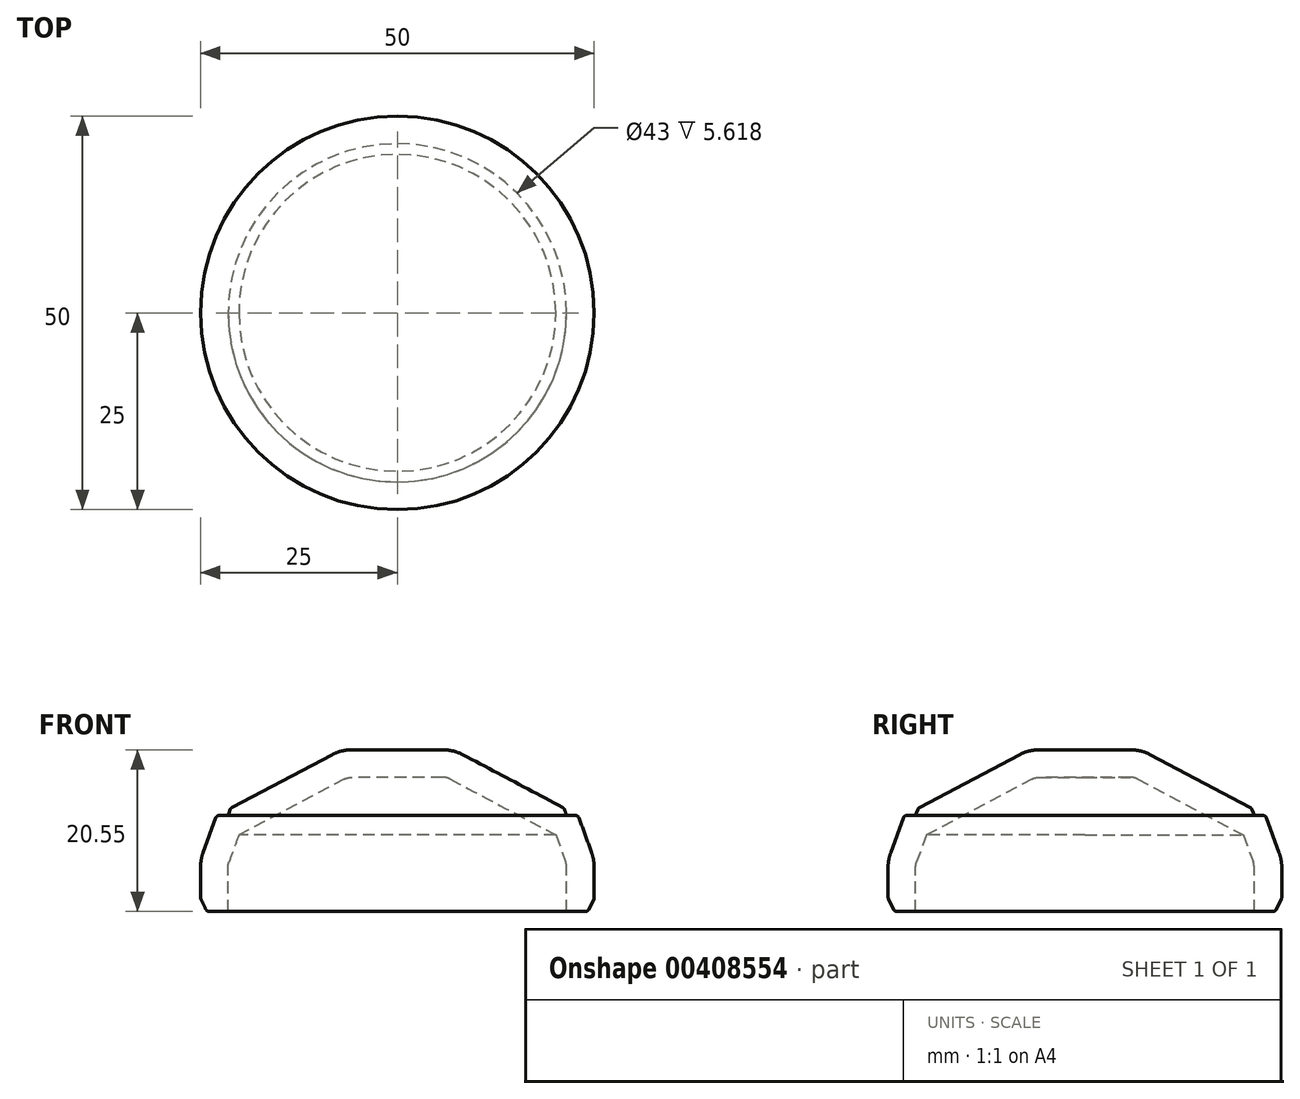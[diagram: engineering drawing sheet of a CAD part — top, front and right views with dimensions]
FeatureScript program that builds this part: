
annotation { "Feature Type Name" : "Feature", "Feature Type Description" : "" }
export const myFeature = defineFeature(function(context is Context, id is Id, definition is map)
    precondition{}
    {
        {
            var Q0;
            Q0=qCreatedBy(makeId("Front.planeOp"),FACE);
            var sketch = newSketch(context, id + "F0", { "sketchPlane" : qUnion([Q0])});
            skLineSegment(sketch, "E0", {"start": v(0, 22.04) * mm, "end": v(0, -27.86) * mm, "construction": true});
            skLineSegment(sketch, "E1", {"start": v(0, 0) * mm, "end": v(-5.75, 0) * mm});
            skArc(sketch, "E2", {"start": v(-5.75, 0) * mm, "mid": v(-7.07, -0.16) * mm, "end": v(-8.31, -0.63) * mm});
            skLineSegment(sketch, "E3", {"start": v(-8.31, -0.63) * mm, "end": v(-20.98, -7.3) * mm});
            skLineSegment(sketch, "E4", {"start": v(-23.08, -8.68) * mm, "end": v(-24.67, -13.05) * mm});
            skLineSegment(sketch, "E5", {"start": v(-25, -14.93) * mm, "end": v(-25, -20.55) * mm});
            skLineSegment(sketch, "E6", {"start": v(-25, -20.55) * mm, "end": v(0, -20.55) * mm});
            skLineSegment(sketch, "E7", {"start": v(0, -20.55) * mm, "end": v(0, 0) * mm});
            skLineSegment(sketch, "E8", {"start": v(-22.6, -8.35) * mm, "end": v(-21.85, -8.35) * mm});
            skLineSegment(sketch, "E9", {"start": v(-21.38, -8.02) * mm, "end": v(-21.22, -7.58) * mm});
            skPoint(sketch, "E10.visualSharp", {"position": v(-21.5, -8.35) * mm});
            skArc(sketch, "E10.filletArc", {"start": v(-21.85, -8.35) * mm, "mid": v(-21.56, -8.26) * mm, "end": v(-21.38, -8.02) * mm});
            skPoint(sketch, "E11.visualSharp", {"position": v(-21.15, -7.4) * mm});
            skArc(sketch, "E11.filletArc", {"start": v(-20.98, -7.3) * mm, "mid": v(-21.13, -7.42) * mm, "end": v(-21.22, -7.58) * mm});
            skPoint(sketch, "E12.visualSharp", {"position": v(-22.96, -8.35) * mm});
            skArc(sketch, "E12.filletArc", {"start": v(-22.6, -8.35) * mm, "mid": v(-22.9, -8.44) * mm, "end": v(-23.08, -8.68) * mm});
            skPoint(sketch, "E13.visualSharp", {"position": v(-25, -13.96) * mm});
            skArc(sketch, "E13.filletArc", {"start": v(-24.67, -13.05) * mm, "mid": v(-24.92, -13.97) * mm, "end": v(-25, -14.93) * mm});
            skSolve(sketch);
        }
        {
            var Q0;
            Q0 = qSketchRegion(id + "F0", true);
            var Q1;
            Q1=sQuery(id+"F0.wireOp",EDGE,"E0");
            revolve(context, id + "F1", {"entities" : qUnion([Q0]), "axis" : qUnion([Q1]), "revolveType" : RevolveType.FULL});
        }
        {
            var Q0;
            Q0=makeQuery(id+"F1.opRevolve","SWEPT_FACE",FACE,{"disambiguationData":[OSD([sQuery(id+"F0.wireOp",EDGE,"E6")])]});
            shell(context, id + "F2", {"entities" : qUnion([Q0]), "thickness" : 3.5 * mm});
        }
        {
            var Q0;
            Q0=makeQuery(id+"F1.opRevolve","SWEPT_EDGE",EDGE,{"disambiguationData":[OSD([sQuery(id+"F0.wireOp",EDGE,"E5"),sQuery(id+"F0.wireOp",EDGE,"E6")])]});
            chamfer(context, id + "F3", {"entities" : qUnion([Q0]), "chamferType" : ChamferType.TWO_OFFSETS, "width1" : 1.7 * mm, "oppositeDirection" : false, "width2" : .8 * mm, "tangentPropagation" : true});
        }
        {
            var Q0;
            {var subQ0=sQuery(id+"F0.wireOp",EDGE,"E6");Q0=makeQuery(id+"F3.opChamfer","BLEND_EDGE",EDGE,{"blendedFrom":[makeQuery(id+"F1.opRevolve","SWEPT_EDGE",EDGE,{"disambiguationData":[OSD([sQuery(id+"F0.wireOp",EDGE,"E5"),subQ0])]}),makeQuery(id+"F1.opRevolve","SWEPT_FACE",FACE,{"disambiguationData":[OSD([subQ0])]})],"blendedInto":[makeQuery(id+"F1.opRevolve","SWEPT_FACE",FACE,{"disambiguationData":[OSD([subQ0])]})]});}
            var Q1;
            {var subQ0=sQuery(id+"F0.wireOp",EDGE,"E5");Q1=makeQuery(id+"F3.opChamfer","BLEND_EDGE",EDGE,{"blendedFrom":[makeQuery(id+"F1.opRevolve","SWEPT_EDGE",EDGE,{"disambiguationData":[OSD([subQ0,sQuery(id+"F0.wireOp",EDGE,"E6")])]}),makeQuery(id+"F1.opRevolve","SWEPT_FACE",FACE,{"disambiguationData":[OSD([subQ0])]})],"blendedInto":[makeQuery(id+"F1.opRevolve","SWEPT_FACE",FACE,{"disambiguationData":[OSD([subQ0])]})]});}
            fillet(context, id + "F4", {"entities" : qUnion([Q0, Q1]), "radius" : 0.5 * mm, "tangentPropagation" : true, "allowEdgeOverflow" : false});
        }
    });
